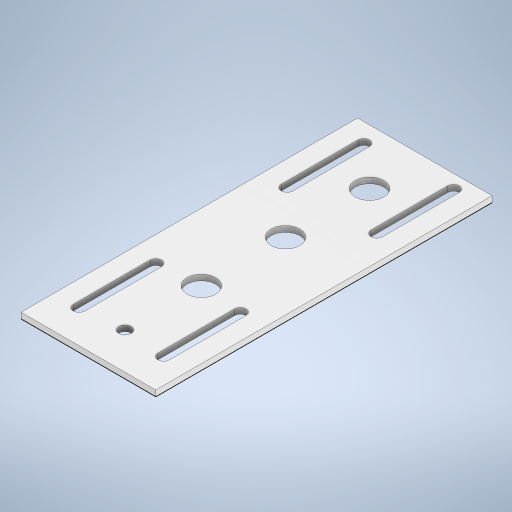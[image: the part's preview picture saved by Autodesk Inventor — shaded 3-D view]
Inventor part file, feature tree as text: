
AUTODESK INVENTOR PART (.ipt)
format: ipt  version: 2023 (Build 270158000, 158)  size: 298,496 bytes
history: native  units: in
note: dims shown in document units (in); Inventor stores cm internally (conversion verified against a paired STEP export)
features: sketch x3, extrude x3
ambient origin geometry x8: Origin, YZ Plane, XZ Plane, XY Plane, X Axis, Y Axis, Z Axis, Center Point
bodies: Solid1 (feature_tree)
feature tree (6):
  sketch  "Sketch1"  dims[d0=2.7559in d1=6.8898in]
  sketch  "Sketch2"  dims[d3=0.5906in d5=0.1181in d6=0.0in]
  extrude  "Extrusion1"  Depth=6.8898in
  extrude  "Extrusion2"  Depth=0.1181in TaperAngle=0.0deg
  extrude  "Extrusion3"  TaperAngle=0.0deg  [1 undecoded]
  sketch  "Sketch6"  dims[d7=0.3937in d8=0.0in d9=0.0in d11=0.3937in d12=0.0in d13=1.5748in d14=1.5748in d15=1.5748in d16=1.5748in d19=0.2362in d20=0.2362in d21=0.2362in d22=0.2362in d23=0.5906in d24=0.5906in d27=2.7559in d28=6.8898in d29=0.3937in d30=0.3937in d31=0.3937in d32=0.3937in d33=1.378in d34=1.378in d35=1.378in d36=1.1319in d37=1.7224in d38=1.7224in d39=0.2559in d40=1.378in d41=0.748in d42=0.6201in d10=0.0344in]
note: 1 required parameter value undecoded (feature->parameter linkage not recoverable at this tier; creation-order binding heuristic only, values carry confidence <= 0.55)
